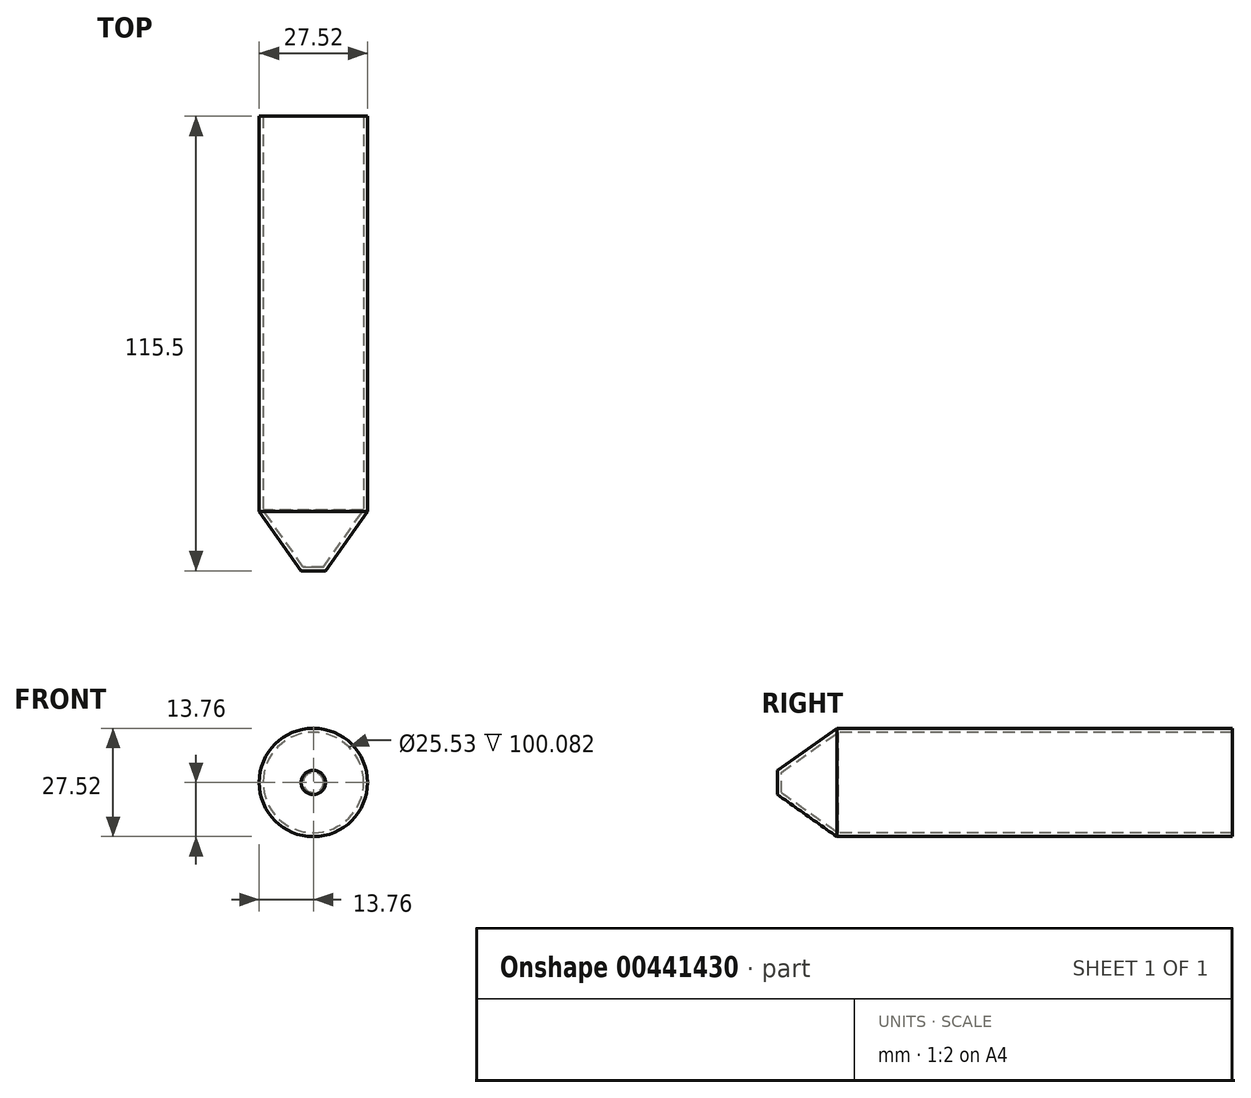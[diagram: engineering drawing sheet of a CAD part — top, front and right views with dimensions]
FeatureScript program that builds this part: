
annotation { "Feature Type Name" : "Feature", "Feature Type Description" : "" }
export const myFeature = defineFeature(function(context is Context, id is Id, definition is map)
    precondition{}
    {
        {
            var Q0;
            Q0=qCreatedBy(makeId("Top.planeOp"),FACE);
            var sketch = newSketch(context, id + "F0", { "sketchPlane" : qUnion([Q0])});
            skLineSegment(sketch, "E0", {"start": v(0, 0) * mm, "end": v(3.08, 0) * mm});
            skLineSegment(sketch, "E1", {"start": v(3.07, 0) * mm, "end": v(13.76, 15.1) * mm});
            skLineSegment(sketch, "E2", {"start": v(13.76, 15.1) * mm, "end": v(13.76, 115.5) * mm});
            skLineSegment(sketch, "E3", {"start": v(3.08, 0) * mm, "end": v(13.76, 0) * mm, "construction": true});
            skLineSegment(sketch, "E4.0", {"start": v(12.76, 15.42) * mm, "end": v(12.76, 115.5) * mm});
            skLineSegment(sketch, "E4.1", {"start": v(2.56, 1) * mm, "end": v(12.76, 15.42) * mm});
            skLineSegment(sketch, "E4.2", {"start": v(0, 1) * mm, "end": v(2.56, 1) * mm});
            skLineSegment(sketch, "E5", {"start": v(0, 0) * mm, "end": v(0, 1) * mm});
            skLineSegment(sketch, "E6", {"start": v(12.76, 115.5) * mm, "end": v(13.76, 115.5) * mm});
            skSolve(sketch);
        }
        {
            var Q0;
            Q0=qSketchRegion(id+"F0",true);
            var Q1;
            Q1=sQuery(id+"F0.wireOp",EDGE,"E5");
            revolve(context, id + "F1", {"entities" : qUnion([Q0]), "axis" : qUnion([Q1]), "revolveType" : RevolveType.FULL});
        }
    });
